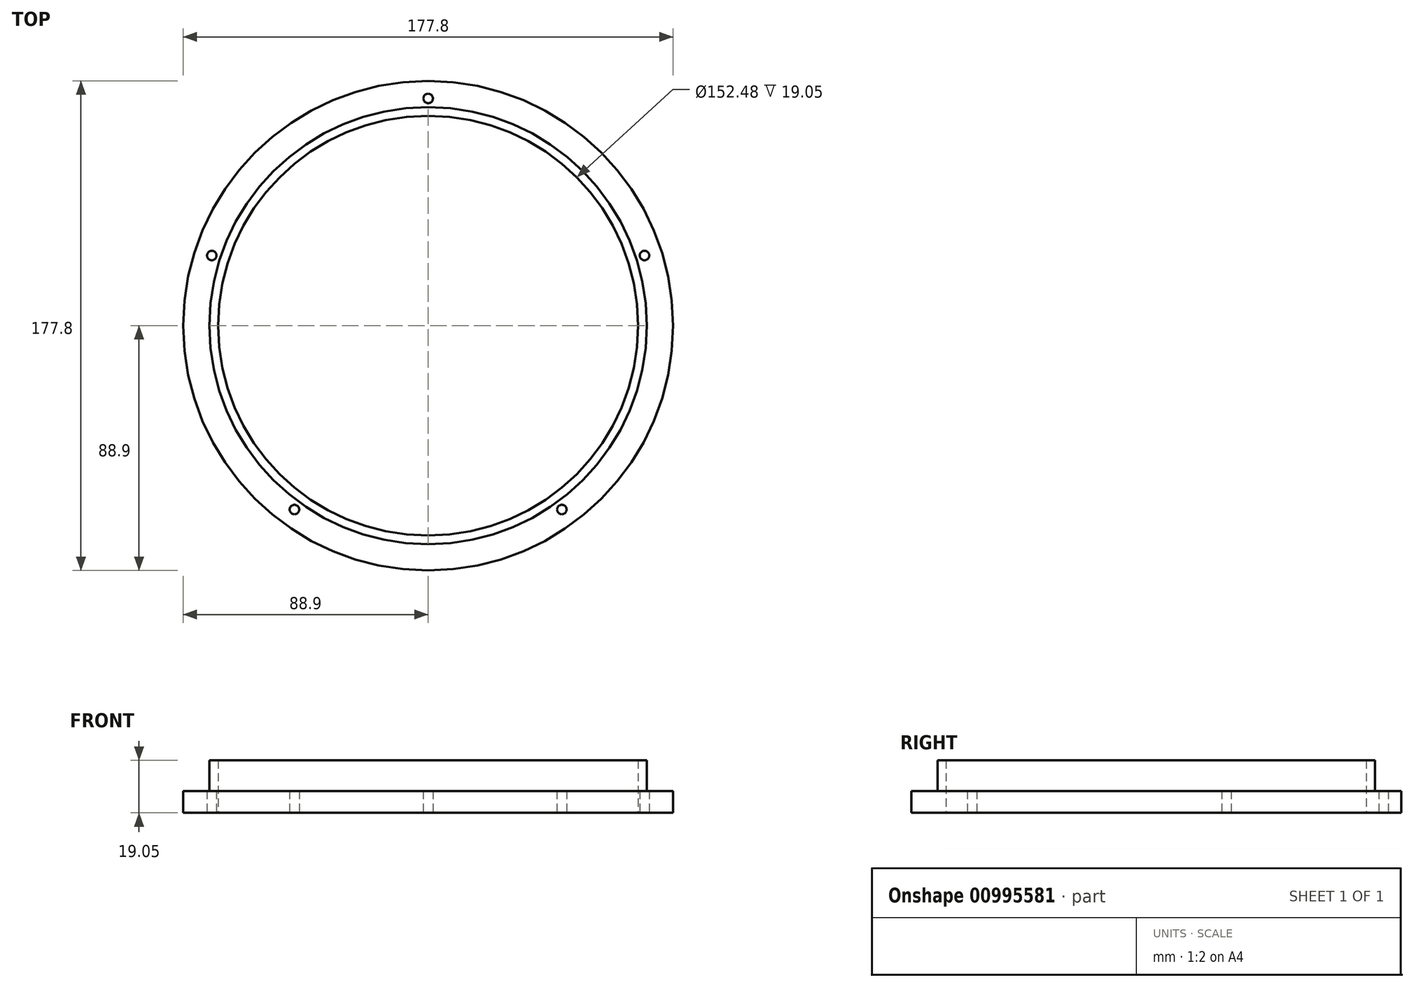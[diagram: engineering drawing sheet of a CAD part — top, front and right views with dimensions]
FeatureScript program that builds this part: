
annotation { "Feature Type Name" : "Feature", "Feature Type Description" : "" }
export const myFeature = defineFeature(function(context is Context, id is Id, definition is map)
    precondition{}
    {
        {
            var Q0;
            Q0=qCreatedBy(makeId("Top.planeOp"),FACE);
            var sketch = newSketch(context, id + "F0", { "sketchPlane" : qUnion([Q0])});
            skCircle(sketch, "E0", {"center": v(0, 0) * mm, "radius": 76.24 * mm});
            skCircle(sketch, "E1", {"center": v(0, 0) * mm, "radius": 88.9 * mm});
            skCircle(sketch, "E2", {"center": v(0, 0) * mm, "radius": 82.55 * mm, "construction": true});
            skCircle(sketch, "E3", {"center": v(0, 82.55) * mm, "radius": 1.73 * mm});
            skCircle(sketch, "E4.1.0", {"center": v(-78.5, 25.5) * mm, "radius": 1.73 * mm});
            skCircle(sketch, "E4.2.0", {"center": v(-48.52, -66.78) * mm, "radius": 1.73 * mm});
            skCircle(sketch, "E4.3.0", {"center": v(48.52, -66.78) * mm, "radius": 1.73 * mm});
            skCircle(sketch, "E4.4.0", {"center": v(78.5, 25.5) * mm, "radius": 1.73 * mm});
            skCircle(sketch, "E5", {"center": v(0, 0) * mm, "radius": 79.38 * mm});
            skSolve(sketch);
        }
        {
            var Q0;
            Q0=makeQuery(id+"F0.imprint","IMPRINT",FACE,{"disambiguationData":[TD([[makeQuery(id+"F0.imprint","IMPRINT",EDGE,{"derivedFrom":sQuery(id+"F0.wireOp",EDGE,"E0")}),-1.0]])]});
            var Q1;
            Q1=makeQuery(id+"F0.imprint","IMPRINT",FACE,{"disambiguationData":[TD([[makeQuery(id+"F0.imprint","IMPRINT",EDGE,{"derivedFrom":sQuery(id+"F0.wireOp",EDGE,"E1")}),1.0]])]});
            extrude(context, id + "F1", {"entities" : qUnion([Q0, Q1]), "depth" : 7.95 * mm, "offsetDistance" : 25.4 * mm});
        }
        {
            var Q0;
            Q0=makeQuery(id+"F0.imprint","IMPRINT",FACE,{"disambiguationData":[TD([[makeQuery(id+"F0.imprint","IMPRINT",EDGE,{"derivedFrom":sQuery(id+"F0.wireOp",EDGE,"E0")}),-1.0]])]});
            extrude(context, id + "F2", {"entities" : qUnion([Q0]), "operationType" : NewBodyOperationType.ADD, "depth" : 19.05 * mm, "offsetDistance" : 25.4 * mm});
        }
    });
